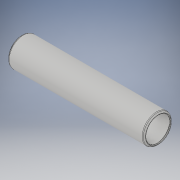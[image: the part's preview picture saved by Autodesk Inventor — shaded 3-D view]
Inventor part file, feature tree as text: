
AUTODESK INVENTOR PART (.ipt)
format: ipt  version: 2019 (Build 230136000, 136)  size: 157,696 bytes
history: native  units: in
note: dims shown in document units (in); Inventor stores cm internally (conversion verified against a paired STEP export)
features: other x42, revolve x1, sketch x1
ambient origin geometry x8: Origin, YZ Plane, XZ Plane, XY Plane, X Axis, Y Axis, Z Axis, Center Point
bodies: Solid1 (feature_tree)
feature tree (44):
  revolve  "Revolution1"  [1 undecoded]
  other  "cp1_XY"
  other  "cp1_YZ"
  other  "cp1_ZX"
  other  "cp1_X"
  other  "cp1_Y"
  other  "cp1_Z"
  other  "cp1_Center"
  other  "cp2_XY"
  other  "cp2_YZ"
  other  "cp2_ZX"
  other  "cp2_X"
  other  "cp2_Y"
  other  "cp2_Z"
  other  "cp2_Center"
  other  "cp3_XY"
  other  "cp3_YZ"
  other  "cp3_ZX"
  other  "cp3_X"
  other  "cp3_Y"
  other  "cp3_Z"
  other  "cp3_Center"
  other  "cp4_XY"
  other  "cp4_YZ"
  other  "cp4_ZX"
  other  "cp4_X"
  other  "cp4_Y"
  other  "cp4_Z"
  other  "cp4_Center"
  other  "tube_front_XY"
  other  "tube_front_YZ"
  other  "tube_front_ZX"
  other  "tube_front_X"
  other  "tube_front_Y"
  other  "tube_front_Z"
  other  "tube_front_Center"
  other  "tube_rear_XY"
  other  "tube_rear_YZ"
  other  "tube_rear_ZX"
  other  "tube_rear_X"
  other  "tube_rear_Y"
  other  "tube_rear_Z"
  other  "tube_rear_Center"
  sketch  "Sketch_1"  dims[d0=360.0deg]
note: 1 required parameter value undecoded (feature->parameter linkage not recoverable at this tier; creation-order binding heuristic only, values carry confidence <= 0.55)
